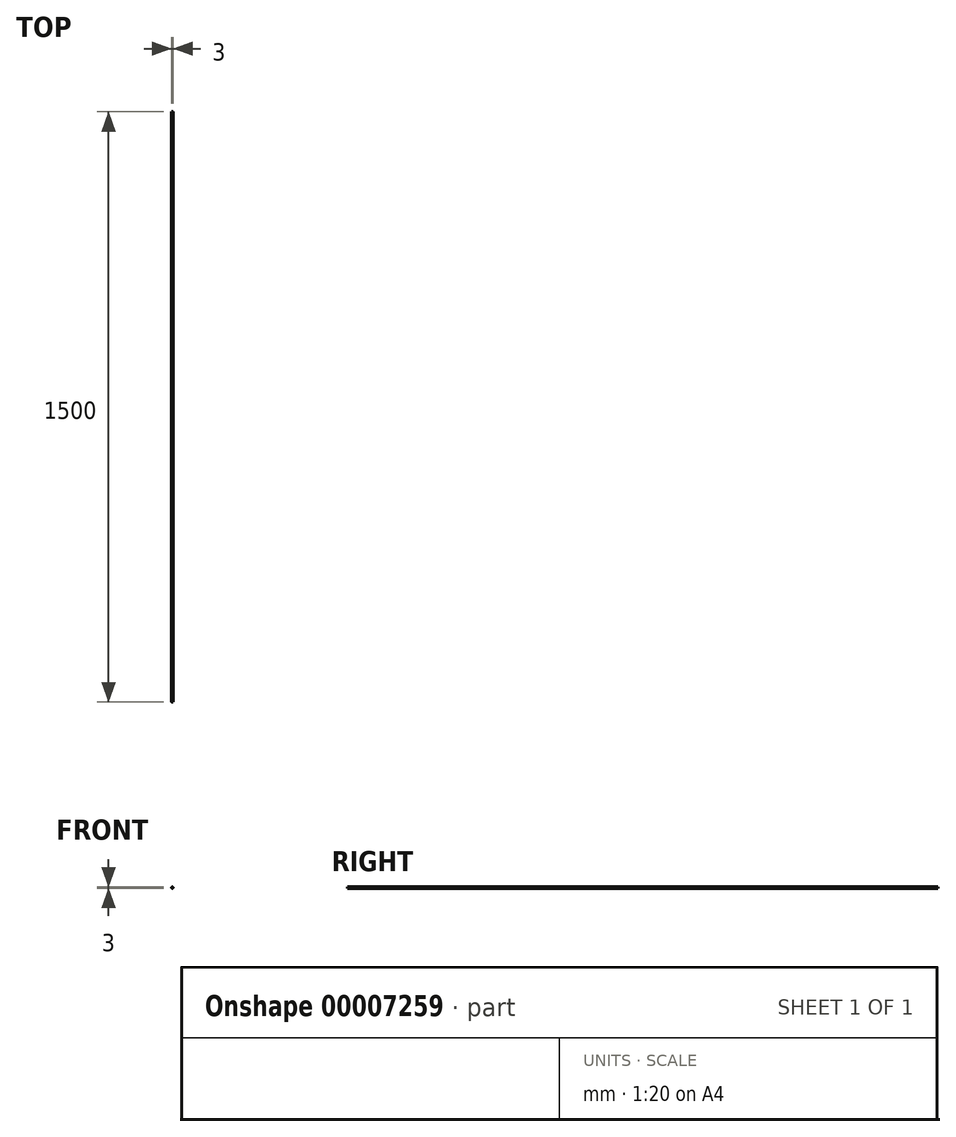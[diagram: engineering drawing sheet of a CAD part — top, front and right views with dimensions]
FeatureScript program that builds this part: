
annotation { "Feature Type Name" : "Feature", "Feature Type Description" : "" }
export const myFeature = defineFeature(function(context is Context, id is Id, definition is map)
    precondition{}
    {
        {
            var Q0;
            Q0=qCreatedBy(makeId("Front.planeOp"),FACE);
            var sketch = newSketch(context, id + "F0", { "sketchPlane" : qUnion([Q0])});
            skCircle(sketch, "E0", {"center": v(0, 0) * mm, "radius": 1.5 * mm});
            skSolve(sketch);
        }
        {
            var Q0;
            Q0=makeQuery(id+"F0.imprint","IMPRINT",FACE,{"disambiguationData":[TD([[makeQuery(id+"F0.imprint","IMPRINT",EDGE,{"derivedFrom":sQuery(id+"F0.wireOp",EDGE,"E0")}),1.0]])]});
            extrude(context, id + "F1", {"entities" : qUnion([Q0]), "depth" : 1500 * mm});
        }
    });
